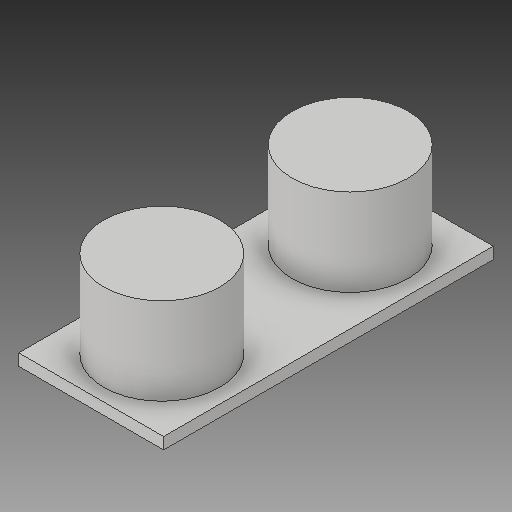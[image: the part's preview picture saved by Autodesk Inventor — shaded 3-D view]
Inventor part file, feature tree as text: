
AUTODESK INVENTOR PART (.ipt)
format: ipt  version: 2018 (Build 220112000, 112)  size: 116,224 bytes
history: native  units: mm
features: extrude x2, sketch x2
ambient origin geometry x8: Origin, YZ Plane, XZ Plane, XY Plane, X Axis, Y Axis, Z Axis, Center Point
bodies: Solid1 (feature_tree)
feature tree (4):
  extrude  "Extrusion1"  Depth=45.5mm
  extrude  "Extrusion2"  Depth=12.0mm
  sketch  "Sketch1"  dims[d0=20.0mm d1=45.5mm]
  sketch  "Sketch2"  dims[d2=1.6mm d3=0.0mm d4=21.0mm d5=8.0mm d6=16.0mm d7=13.0mm d8=16.0mm d9=12.0mm d10=0.0mm]
